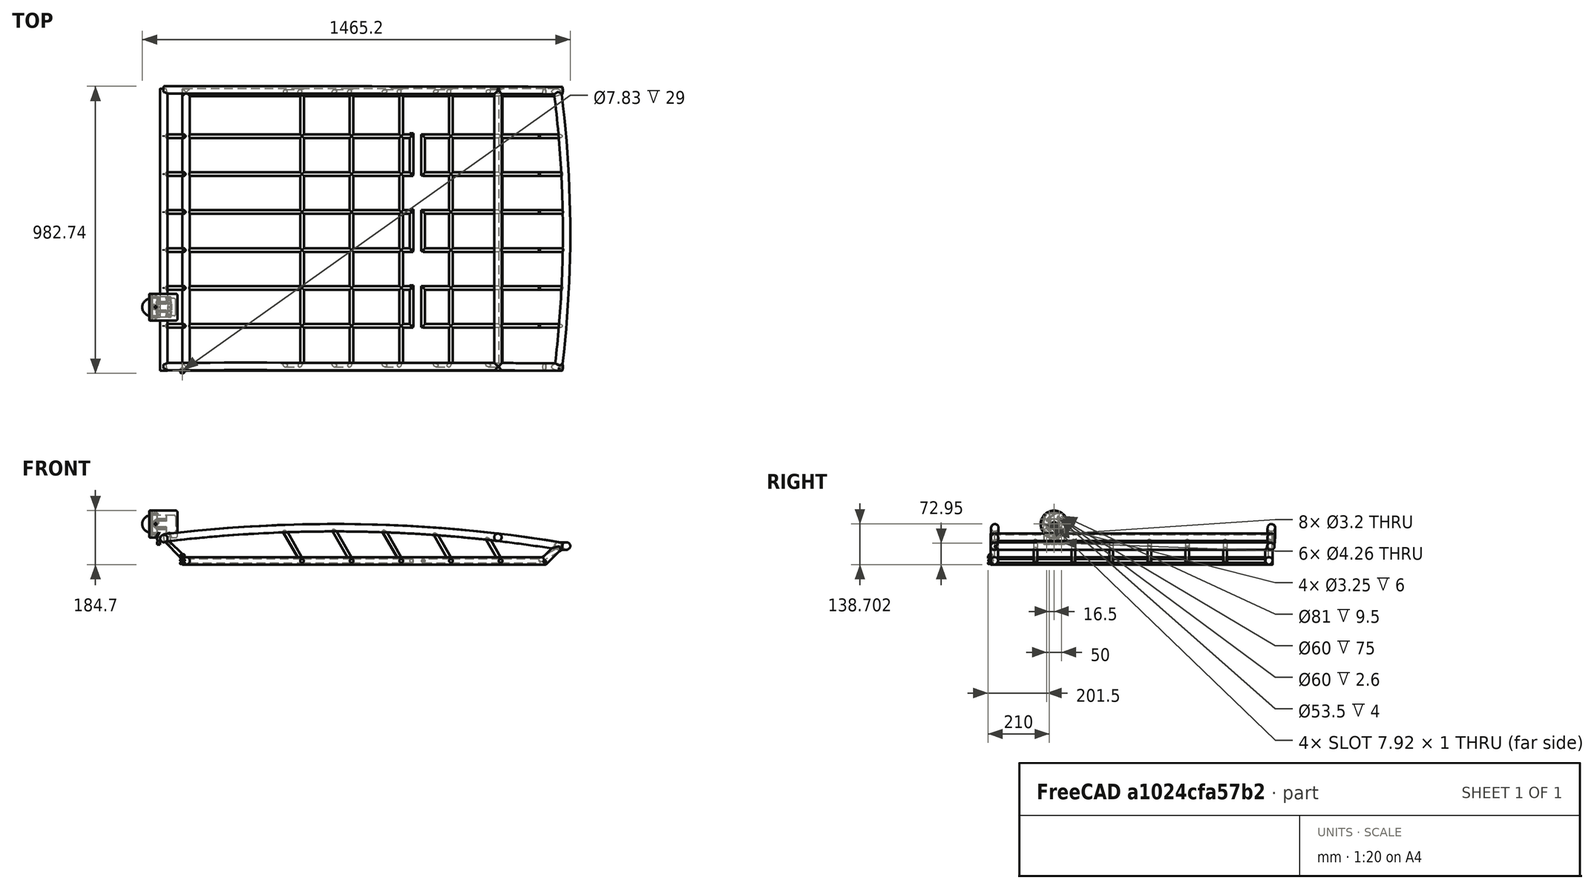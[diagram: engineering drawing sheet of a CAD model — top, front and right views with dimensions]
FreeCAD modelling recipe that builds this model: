
FCSTD DOCUMENT  (FreeCAD 1.0R39285 (Git))
Label: boltCameraMount
License: All rights reserved
LicenseURL: https://en.wikipedia.org/wiki/All_rights_reserved
objects: Part::Cylinder×65, Part::MultiFuse×23, Part::Feature×23, Sketcher::SketchObject×10, Part::Extrusion×10, Part::Cut×10, Part::Torus×3, Part::FeaturePython×2, App::Part×2, Part::Mirroring×2, Part::Sphere×2, Part::Fillet×2
note: 162 computed .brp shape members not serialized (recipe doc carries the construction recipe); baked Part::Feature solids carry a one-line shape summary decoded from their .brp

FEATURE [Part::Cylinder] Cylinder  label="base00"
  Angle = 360
  AttacherType = Attacher::AttachEngine3D
  FirstAngle = 0
  Height = 965.2
  Placement = pos=(12.7,0,0) rot=(-0.57735,0.57735,0.57735;2.0944rad)
  Radius = 12.7
  SecondAngle = 0
FEATURE [Part::Cylinder] Cylinder002  label="base02"
  Angle = 360
  AttacherType = Attacher::AttachEngine3D
  FirstAngle = 0
  Height = 1244.6
  Placement = pos=(0,12.7,0) rot=(0,1,0;1.5708rad)
  Radius = 12.7
  SecondAngle = 0
FEATURE [Part::Cylinder] Cylinder003  label="base03"
  Angle = 360
  AttacherType = Attacher::AttachEngine3D
  FirstAngle = 0
  Height = 1244.6
  Placement = pos=(0,952.5,0) rot=(0,1,0;1.5708rad)
  Radius = 12.7
  SecondAngle = 0
FEATURE [Part::Cylinder] Cylinder004  label="mount01"
  Angle = 360
  AttacherType = Attacher::AttachEngine3D
  FirstAngle = 0
  Height = 76.2
  Placement = pos=(1235.62,12.7,-3.72) rot=(0.382683,0,0.92388;3.14159rad)
  Radius = 12.7
  SecondAngle = 0
FEATURE [Part::Cylinder] Cylinder005  label="mount002"
  Angle = 360
  AttacherType = Attacher::AttachEngine3D
  FirstAngle = 0
  Height = 76.2
  Placement = pos=(1235.62,952.5,-3.72) rot=(0.382683,0,0.92388;3.14159rad)
  Radius = 12.7
  SecondAngle = 0
FEATURE [Part::Cylinder] Cylinder006  label="base004"
  Angle = 360
  AttacherType = Attacher::AttachEngine3D
  FirstAngle = 0
  Height = 965.2
  Placement = pos=(-63.5,0,76.2) rot=(-0.57735,0.57735,0.57735;2.0944rad)
  Radius = 12.7
  SecondAngle = 0
FEATURE [Part::Cylinder] Cylinder007  label="base005"
  Angle = 360
  AttacherType = Attacher::AttachEngine3D
  FirstAngle = 0
  Height = 965.2
  Placement = pos=(1089.2,0,0) rot=(0.57735,-0.57735,-0.57735;4.18879rad)
  Radius = 6.35
  SecondAngle = 0
FEATURE [Part::Cylinder] Cylinder008  label="base006"
  Angle = 360
  AttacherType = Attacher::AttachEngine3D
  FirstAngle = 0
  Height = 965.2
  Placement = pos=(919.2,0,0) rot=(0.57735,-0.57735,-0.57735;4.18879rad)
  Radius = 6.35
  SecondAngle = 0
FEATURE [Part::Cylinder] Cylinder009  label="base007"
  Angle = 360
  AttacherType = Attacher::AttachEngine3D
  FirstAngle = 0
  Height = 965.2
  Placement = pos=(749.2,0,0) rot=(0.57735,-0.57735,-0.57735;4.18879rad)
  Radius = 6.35
  SecondAngle = 0
FEATURE [Part::Cylinder] Cylinder010  label="base008"
  Angle = 360
  AttacherType = Attacher::AttachEngine3D
  FirstAngle = 0
  Height = 965.2
  Placement = pos=(579.2,0,0) rot=(0.57735,-0.57735,-0.57735;4.18879rad)
  Radius = 6.35
  SecondAngle = 0
FEATURE [Part::Cylinder] Cylinder011  label="base009"
  Angle = 360
  AttacherType = Attacher::AttachEngine3D
  FirstAngle = 0
  Height = 965.2
  Placement = pos=(409.2,0,0) rot=(0.57735,-0.57735,-0.57735;4.18879rad)
  Radius = 6.35
  SecondAngle = 0
FEATURE [Part::Cylinder] Cylinder012  label="base010"
  Angle = 360
  AttacherType = Attacher::AttachEngine3D
  FirstAngle = 0
  Height = 790
  Placement = pos=(0,149.7,0) rot=(0,1,0;1.5708rad)
  Radius = 6.35
  SecondAngle = 0
FEATURE [Part::Cylinder] Cylinder013  label="base011"
  Angle = 360
  AttacherType = Attacher::AttachEngine3D
  FirstAngle = 0
  Height = 790
  Placement = pos=(0,279.7,0) rot=(0,1,0;1.5708rad)
  Radius = 6.35
  SecondAngle = 0
FEATURE [Part::Cylinder] Cylinder014  label="base012"
  Angle = 360
  AttacherType = Attacher::AttachEngine3D
  FirstAngle = 0
  Height = 790
  Placement = pos=(0,409.7,0) rot=(0,1,0;1.5708rad)
  Radius = 6.35
  SecondAngle = 0
FEATURE [Part::Cylinder] Cylinder015  label="base013"
  Angle = 360
  AttacherType = Attacher::AttachEngine3D
  FirstAngle = 0
  Height = 790
  Placement = pos=(0,539.7,0) rot=(0,1,0;1.5708rad)
  Radius = 6.35
  SecondAngle = 0
FEATURE [Part::Cylinder] Cylinder016  label="base014"
  Angle = 360
  AttacherType = Attacher::AttachEngine3D
  FirstAngle = 0
  Height = 790
  Placement = pos=(0,669.7,0) rot=(0,1,0;1.5708rad)
  Radius = 6.35
  SecondAngle = 0
FEATURE [Part::Cylinder] Cylinder017  label="base015"
  Angle = 360
  AttacherType = Attacher::AttachEngine3D
  FirstAngle = 0
  Height = 790
  Placement = pos=(0,799.7,0) rot=(0,1,0;1.5708rad)
  Radius = 6.35
  SecondAngle = 0
FEATURE [Part::Cylinder] Cylinder018  label="base016"
  Angle = 360
  AttacherType = Attacher::AttachEngine3D
  FirstAngle = 0
  Height = 141
  Placement = pos=(784.2,148,0) rot=(0.57735,-0.57735,-0.57735;4.18879rad)
  Radius = 6.35
  SecondAngle = 0
FEATURE [Part::Cylinder] Cylinder019  label="base017"
  Angle = 360
  AttacherType = Attacher::AttachEngine3D
  FirstAngle = 0
  Height = 141
  Placement = pos=(784.2,408,0) rot=(0.57735,-0.57735,-0.57735;4.18879rad)
  Radius = 6.35
  SecondAngle = 0
FEATURE [Part::Cylinder] Cylinder020  label="base018"
  Angle = 360
  AttacherType = Attacher::AttachEngine3D
  FirstAngle = 0
  Height = 141
  Placement = pos=(784.2,668,0) rot=(0.57735,-0.57735,-0.57735;4.18879rad)
  Radius = 6.35
  SecondAngle = 0
FEATURE [Part::Cylinder] Cylinder021  label="base019"
  Angle = 360
  AttacherType = Attacher::AttachEngine3D
  FirstAngle = 0
  Height = 400
  Placement = pos=(0,149.7,0) rot=(0,1,0;1.5708rad)
  Radius = 6.35
  SecondAngle = 0
FEATURE [Part::Cylinder] Cylinder022  label="base020"
  Angle = 360
  AttacherType = Attacher::AttachEngine3D
  FirstAngle = 0
  Height = 400
  Placement = pos=(0,279.7,0) rot=(0,1,0;1.5708rad)
  Radius = 6.35
  SecondAngle = 0
FEATURE [Part::Cylinder] Cylinder023  label="base021"
  Angle = 360
  AttacherType = Attacher::AttachEngine3D
  FirstAngle = 0
  Height = 400
  Placement = pos=(0,409.7,0) rot=(0,1,0;1.5708rad)
  Radius = 6.35
  SecondAngle = 0
FEATURE [Part::Cylinder] Cylinder024  label="base022"
  Angle = 360
  AttacherType = Attacher::AttachEngine3D
  FirstAngle = 0
  Height = 400
  Placement = pos=(0,539.7,0) rot=(0,1,0;1.5708rad)
  Radius = 6.35
  SecondAngle = 0
FEATURE [Part::Cylinder] Cylinder025  label="base023"
  Angle = 360
  AttacherType = Attacher::AttachEngine3D
  FirstAngle = 0
  Height = 400
  Placement = pos=(0,669.7,0) rot=(0,1,0;1.5708rad)
  Radius = 6.35
  SecondAngle = 0
FEATURE [Part::Cylinder] Cylinder026  label="base024"
  Angle = 360
  AttacherType = Attacher::AttachEngine3D
  FirstAngle = 0
  Height = 400
  Placement = pos=(0,799.7,0) rot=(0,1,0;1.5708rad)
  Radius = 6.35
  SecondAngle = 0
FEATURE [Part::Cylinder] Cylinder027  label="base025"
  Angle = 360
  AttacherType = Attacher::AttachEngine3D
  FirstAngle = 0
  Height = 141
  Placement = pos=(0,665,0) rot=(0.57735,-0.57735,-0.57735;4.18879rad)
  Radius = 6.35
  SecondAngle = 0
FEATURE [Part::Cylinder] Cylinder028  label="base026"
  Angle = 360
  AttacherType = Attacher::AttachEngine3D
  FirstAngle = 0
  Height = 141
  Placement = pos=(0,405,0) rot=(0.57735,-0.57735,-0.57735;4.18879rad)
  Radius = 6.35
  SecondAngle = 0
FEATURE [Part::Cylinder] Cylinder029  label="base027"
  Angle = 360
  AttacherType = Attacher::AttachEngine3D
  FirstAngle = 0
  Height = 141
  Placement = pos=(0,145,0) rot=(0.57735,-0.57735,-0.57735;4.18879rad)
  Radius = 6.35
  SecondAngle = 0
FEATURE [Part::Cylinder] Cylinder030  label="Cylinder"
  Angle = 360
  AttacherType = Attacher::AttachEngine3D
  FirstAngle = 0
  Height = 124.3
  Placement = pos=(409,19,0) rot=(0,-1,0;0.523599rad)
  Radius = 6.35
  SecondAngle = 0
FEATURE [Part::Cylinder] Cylinder031
  Angle = 360
  AttacherType = Attacher::AttachEngine3D
  FirstAngle = 0
  Height = 131.3
  Placement = pos=(579,19,0) rot=(0,-1,0;0.523599rad)
  Radius = 6.35
  SecondAngle = 0
FEATURE [Part::Cylinder] Cylinder032
  Angle = 360
  AttacherType = Attacher::AttachEngine3D
  FirstAngle = 0
  Height = 124.3
  Placement = pos=(749,19,0) rot=(0,-1,0;0.523599rad)
  Radius = 6.35
  SecondAngle = 0
FEATURE [Part::Cylinder] Cylinder033
  Angle = 360
  AttacherType = Attacher::AttachEngine3D
  FirstAngle = 0
  Height = 117.3
  Placement = pos=(919,19,0) rot=(0,-1,0;0.523599rad)
  Radius = 6.35
  SecondAngle = 0
FEATURE [Part::Cylinder] Cylinder034
  Angle = 360
  AttacherType = Attacher::AttachEngine3D
  FirstAngle = 0
  Height = 96.3
  Placement = pos=(1089,19,0) rot=(0,-1,0;0.523599rad)
  Radius = 6.35
  SecondAngle = 0
FEATURE [Part::Cylinder] Cylinder035
  Angle = 360
  AttacherType = Attacher::AttachEngine3D
  FirstAngle = 0
  Height = 124.3
  Placement = pos=(409,19,0) rot=(0,-1,0;0.523599rad)
  Radius = 6.35
  SecondAngle = 0
FEATURE [Part::Cylinder] Cylinder036
  Angle = 360
  AttacherType = Attacher::AttachEngine3D
  FirstAngle = 0
  Height = 131.3
  Placement = pos=(579,19,0) rot=(0,-1,0;0.523599rad)
  Radius = 6.35
  SecondAngle = 0
FEATURE [Part::Cylinder] Cylinder037
  Angle = 360
  AttacherType = Attacher::AttachEngine3D
  FirstAngle = 0
  Height = 124.3
  Placement = pos=(749,19,0) rot=(0,-1,0;0.523599rad)
  Radius = 6.35
  SecondAngle = 0
FEATURE [Part::Cylinder] Cylinder038
  Angle = 360
  AttacherType = Attacher::AttachEngine3D
  FirstAngle = 0
  Height = 117.3
  Placement = pos=(919,19,0) rot=(0,-1,0;0.523599rad)
  Radius = 6.35
  SecondAngle = 0
FEATURE [Part::Cylinder] Cylinder039
  Angle = 360
  AttacherType = Attacher::AttachEngine3D
  FirstAngle = 0
  Height = 96.3
  Placement = pos=(1089,19,0) rot=(0,-1,0;0.523599rad)
  Radius = 6.35
  SecondAngle = 0
FEATURE [Part::Cylinder] Cylinder040 .. Cylinder044  x5 (patterned run collapsed; names and placements below)
  Angle = 360
  AttacherType = Attacher::AttachEngine3D
  FirstAngle = 0
  Height = 124.3
  Radius = 6.35
  SecondAngle = 0
  placements: 5 in arithmetic series — first pos=(17.6777,152.7,-3.53553) rot=(0,-1,0;0.785398rad), step (0,130,0), last pos=(17.6777,672.7,-3.53553) rot=(0,-1,0;0.785398rad)
FEATURE [Part::Cylinder] Cylinder045
  Angle = 360
  AttacherType = Attacher::AttachEngine3D
  FirstAngle = 0
  Height = 100.3
  Placement = pos=(17.6777,152.7,-3.53553) rot=(0,-1,0;0.785398rad)
  Radius = 6.35
  SecondAngle = 0
FEATURE [Part::Cylinder] Cylinder046 .. Cylinder050  x5 (patterned run collapsed; names and placements below)
  Angle = 360
  AttacherType = Attacher::AttachEngine3D
  FirstAngle = 0
  Height = 100
  Radius = 6.35
  SecondAngle = 0
  placements: 5 in arithmetic series — first pos=(17.6777,282.7,-3.53553) rot=(0,-1,0;0.785398rad), step (0,130,0), last pos=(17.6777,802.7,-3.53553) rot=(0,-1,0;0.785398rad)
FEATURE [Part::Cylinder] Cylinder051
  Angle = 360
  AttacherType = Attacher::AttachEngine3D
  FirstAngle = 0
  Height = 124.3
  Placement = pos=(17.6777,802.7,-3.53553) rot=(0,-1,0;0.785398rad)
  Radius = 6.35
  SecondAngle = 0
FEATURE [Part::Cylinder] Cylinder052  label="base028"
  Angle = 360
  AttacherType = Attacher::AttachEngine3D
  FirstAngle = 0
  Height = 965.2
  Placement = pos=(1080,0,80.5) rot=(-0.57735,0.57735,0.57735;2.0944rad)
  Radius = 12.7
  SecondAngle = 0
FEATURE [Part::MultiFuse] Fusion001  label="vertical"
  Shapes = -> [Cylinder007,Cylinder008,Cylinder009,Cylinder010,Cylinder011]
FEATURE [Part::MultiFuse] Fusion002  label="horizontal"
  Placement = pos=(0,3,0) rot=(0,0,1;0rad)
  Shapes = -> [Cylinder012,Cylinder013,Cylinder014,Cylinder015,Cylinder016,Cylinder017,Cylinder018,Cylinder019,Cylinder020]
FEATURE [Part::MultiFuse] Fusion003  label="horizontal_front"
  Placement = pos=(824,3,0) rot=(0,0,1;0rad)
  Shapes = -> [Cylinder025,Cylinder026,Cylinder022,Cylinder021,Cylinder023,Cylinder024,Cylinder027,Cylinder029,Cylinder028]
FEATURE [Part::MultiFuse] Fusion004  label="side_bars_1"
  Shapes = -> [Cylinder030,Cylinder031,Cylinder032,Cylinder033,Cylinder034]
FEATURE [Part::MultiFuse] Fusion005  label="side_bars_002"
  Placement = pos=(0,936.4,0) rot=(0,0,1;0rad)
  Shapes = -> [Cylinder035,Cylinder036,Cylinder037,Cylinder038,Cylinder039]
FEATURE [Part::MultiFuse] Fusion006  label="Back_bars"
  Shapes = -> [Cylinder040,Cylinder041,Cylinder042,Cylinder043,Cylinder044,Cylinder051]
FEATURE [Part::MultiFuse] Fusion007  label="front_bar"
  Placement = pos=(1229,0,16) rot=(0,1,0;1.8326rad)
  Shapes = -> [Cylinder045,Cylinder046,Cylinder047,Cylinder048,Cylinder049,Cylinder050]
FEATURE [Part::Torus] Torus
  Angle1 = -180
  Angle2 = 180
  Angle3 = 14.3
  AttacherType = Attacher::AttachEngine3D
  Placement = pos=(-2495,471.5,50.8) rot=(0,0,-1;0.122173rad)
  Radius1 = 3810
  Radius2 = 12.7
FEATURE [Part::Torus] Torus001
  Angle1 = -180
  Angle2 = 180
  Angle3 = 16.28
  AttacherType = Attacher::AttachEngine3D
  Placement = pos=(519.042,-57.4562,-4703.18) rot=(0.533716,0.602162,0.593758;4.10898rad)
  Radius1 = 4817.1
  Radius2 = 12.7
FEATURE [Part::Torus] Torus002
  Angle1 = -180
  Angle2 = 180
  Angle3 = 16.28
  AttacherType = Attacher::AttachEngine3D
  Placement = pos=(519.042,889,-4703.18) rot=(0.533716,0.602162,0.593758;4.10898rad)
  Radius1 = 4817.1
  Radius2 = 12.7
FEATURE [Part::MultiFuse] Fusion  label="out_frame"
  Shapes = -> [Cylinder,Cylinder002,Cylinder003,Cylinder005,Cylinder004,Torus,Cylinder006,Torus001,Torus002,Cylinder052]
FEATURE [Part::MultiFuse] Fusion011  label="Car_frame"
  Shapes = -> [Fusion,Fusion001,Fusion002,Fusion003,Fusion004,Fusion005,Fusion006,Fusion007]
FEATURE [Sketcher::SketchObject] Sketch
  ArcFitTolerance = 1e-06
  FullyConstrained = true
  MakeInternals = false
  Placement = pos=(0,0,0) rot=(1,0,0;1.5708rad)
  sketch-geometry (10):
    g0: ArcOfCircle CenterX=0 CenterY=0 CenterZ=0 NormalX=0 NormalY=0 NormalZ=1 AngleXU=0 Radius=13.25 StartAngle=6.28318 EndAngle=9.42478
    g1: ArcOfCircle CenterX=0 CenterY=0 CenterZ=0 NormalX=0 NormalY=0 NormalZ=1 AngleXU=0 Radius=23 StartAngle=5.8031 EndAngle=9.90486
    g2: LineSegment StartX=-20.4 StartY=-10.6226 StartZ=0 EndX=-23.25 EndY=-10.6226 EndZ=0
    g3: LineSegment StartX=-23.25 StartY=-10.6226 StartZ=0 EndX=-23.25 EndY=-20.6226 EndZ=0
    g4: LineSegment StartX=-23.25 StartY=-20.6226 StartZ=0 EndX=-13.25 EndY=-20.6226 EndZ=0
    g5: LineSegment StartX=20.4 StartY=-10.6226 StartZ=0 EndX=23.25 EndY=-10.6226 EndZ=0
    g6: LineSegment StartX=23.25 StartY=-10.6226 StartZ=0 EndX=23.25 EndY=-20.6226 EndZ=0
    g7: LineSegment StartX=23.25 StartY=-20.6226 StartZ=0 EndX=13.25 EndY=-20.6226 EndZ=0
    g8: LineSegment StartX=13.25 StartY=-20.6226 StartZ=0 EndX=13.25 EndY=-2.78003e-05 EndZ=0
    g9: LineSegment StartX=-13.25 StartY=-20.6226 StartZ=0 EndX=-13.25 EndY=-2.78003e-05 EndZ=0
  constraints (29):
    c: Coincident(g0,g-1)
    c: Coincident(g1,g0)
    c: Coincident(g2,g1)
    c: Horizontal(g2)
    c: Coincident(g3,g2)
    c: Vertical(g3)
    c: Coincident(g4,g3)
    c: Horizontal(g4)
    c: Coincident(g5,g1)
    c: Horizontal(g5)
    c: Coincident(g6,g5)
    c: Vertical(g6)
    c: Coincident(g7,g6)
    c: Horizontal(g7)
    c: Diameter(g0) = 26.5
    c: Diameter(g1) = 46
    c: DistanceY(g3,g3) = 10
    c: DistanceY(g6,g6) = 10
    c: DistanceX(g7,g7) = 10
    c: DistanceX(g4,g4) = 10
    c: Distance(g2,g2) = 2.85
    c: Coincident(g8,g7)
    c: Coincident(g8,g0)
    c: Coincident(g9,g4)
    c: Coincident(g9,g0)
    c: Vertical(g8)
    c: Vertical(g9)
    c: Symmetric(g4,g7,g-2)
    c: DistanceX(g0,g0) = 26.5
FEATURE [Part::Extrusion] Extrude  label="CamHold"
  Base = -> Sketch
  Dir = (0,-1,2e-16)
  DirMode = 2
  FaceMakerClass = Part::FaceMakerBullseye
  FaceMakerMode = 3
  LengthFwd = 20
  LengthRev = 0
  Placement = pos=(0,-15,0) rot=(0,0,1;0rad)
  Solid = true
  Symmetric = false
FEATURE [Part::FeaturePython] Tube  # WARN: FeaturePython — macro-defined, semantics opaque (R4)
  AttacherType = Attacher::AttachEngine3D
  Height = 80
  InnerRadius = 30
  OuterRadius = 46
  Placement = pos=(40,-50,50) rot=(0,1,0;4.71239rad)
FEATURE [Part::Cylinder] Cylinder059
  Angle = 360
  AttacherType = Attacher::AttachEngine3D
  FirstAngle = 0
  Height = 150
  Placement = pos=(0,-125,0) rot=(1,0,0;4.71239rad)
  Radius = 13.25
  SecondAngle = 0
FEATURE [Part::Cut] Cut  label="CylinderCam"
  Base = -> Tube
  Refine = true
  Tool = -> Cylinder059
FEATURE [Sketcher::SketchObject] Sketch004
  ArcFitTolerance = 1e-06
  FullyConstrained = true
  MakeInternals = false
  Placement = pos=(0,0,0) rot=(1,0,0;1.5708rad)
  sketch-geometry (10):
    g0: ArcOfCircle CenterX=0 CenterY=0 CenterZ=0 NormalX=0 NormalY=0 NormalZ=1 AngleXU=0 Radius=13.25 StartAngle=6.28319 EndAngle=9.42478
    g1: ArcOfCircle CenterX=0 CenterY=0 CenterZ=0 NormalX=0 NormalY=0 NormalZ=1 AngleXU=0 Radius=23 StartAngle=5.8031 EndAngle=9.90486
    g2: LineSegment StartX=-20.4 StartY=-10.6226 StartZ=0 EndX=-23.25 EndY=-10.6226 EndZ=0
    g3: LineSegment StartX=-23.25 StartY=-10.6226 StartZ=0 EndX=-23.25 EndY=-20.6226 EndZ=0
    g4: LineSegment StartX=-23.25 StartY=-20.6226 StartZ=0 EndX=-13.25 EndY=-20.6226 EndZ=0
    g5: LineSegment StartX=20.4 StartY=-10.6226 StartZ=0 EndX=23.25 EndY=-10.6226 EndZ=0
    g6: LineSegment StartX=23.25 StartY=-10.6226 StartZ=0 EndX=23.25 EndY=-20.6226 EndZ=0
    g7: LineSegment StartX=23.25 StartY=-20.6226 StartZ=0 EndX=13.25 EndY=-20.6226 EndZ=0
    g8: LineSegment StartX=-13.25 StartY=-20.6226 StartZ=0 EndX=-13.25 EndY=-4.29509e-07 EndZ=0
    g9: LineSegment StartX=13.25 StartY=-20.6226 StartZ=0 EndX=13.25 EndY=-3.97031e-07 EndZ=0
  constraints (29):
    c: Coincident(g0,g-1)
    c: Coincident(g1,g0)
    c: Coincident(g2,g1)
    c: Horizontal(g2)
    c: Coincident(g3,g2)
    c: Vertical(g3)
    c: Coincident(g4,g3)
    c: Horizontal(g4)
    c: Coincident(g5,g1)
    c: Horizontal(g5)
    c: Coincident(g6,g5)
    c: Vertical(g6)
    c: Coincident(g7,g6)
    c: Horizontal(g7)
    c: Diameter(g0) = 26.5
    c: Diameter(g1) = 46
    c: DistanceY(g3,g3) = 10
    c: DistanceY(g6,g6) = 10
    c: DistanceX(g7,g7) = 10
    c: DistanceX(g4,g4) = 10
    c: Distance(g2,g2) = 2.85
    c: Coincident(g8,g4)
    c: Coincident(g8,g0)
    c: Coincident(g9,g7)
    c: Coincident(g9,g0)
    c: Vertical(g8)
    c: Vertical(g9)
    c: Symmetric(g4,g7,g-2)
    c: DistanceX(g0,g0) = 26.5
FEATURE [Part::Extrusion] Extrude004  label="CamHold001"
  Base = -> Sketch004
  Dir = (0,-1,2e-16)
  DirMode = 2
  FaceMakerClass = Part::FaceMakerBullseye
  FaceMakerMode = 3
  LengthFwd = 20
  LengthRev = 0
  Placement = pos=(0,-40,0) rot=(0,0,1;0rad)
  Solid = true
  Symmetric = false
FEATURE [Sketcher::SketchObject] Sketch005
  ArcFitTolerance = 1e-06
  FullyConstrained = true
  MakeInternals = false
  Placement = pos=(0,0,0) rot=(1,0,0;1.5708rad)
  sketch-geometry (10):
    g0: ArcOfCircle CenterX=0 CenterY=0 CenterZ=0 NormalX=0 NormalY=0 NormalZ=1 AngleXU=0 Radius=13.25 StartAngle=6.28319 EndAngle=9.42478
    g1: ArcOfCircle CenterX=0 CenterY=0 CenterZ=0 NormalX=0 NormalY=0 NormalZ=1 AngleXU=0 Radius=23 StartAngle=5.8031 EndAngle=9.90486
    g2: LineSegment StartX=-20.4 StartY=-10.6226 StartZ=0 EndX=-23.25 EndY=-10.6226 EndZ=0
    g3: LineSegment StartX=-23.25 StartY=-10.6226 StartZ=0 EndX=-23.25 EndY=-20.6226 EndZ=0
    g4: LineSegment StartX=-23.25 StartY=-20.6226 StartZ=0 EndX=-13.25 EndY=-20.6226 EndZ=0
    g5: LineSegment StartX=20.4 StartY=-10.6226 StartZ=0 EndX=23.25 EndY=-10.6226 EndZ=0
    g6: LineSegment StartX=23.25 StartY=-10.6226 StartZ=0 EndX=23.25 EndY=-20.6226 EndZ=0
    g7: LineSegment StartX=23.25 StartY=-20.6226 StartZ=0 EndX=13.25 EndY=-20.6226 EndZ=0
    g8: LineSegment StartX=-13.25 StartY=-20.6226 StartZ=0 EndX=-13.25 EndY=-4.19512e-07 EndZ=0
    g9: LineSegment StartX=13.25 StartY=-20.6226 StartZ=0 EndX=13.25 EndY=-4.07791e-07 EndZ=0
  constraints (29):
    c: Coincident(g0,g-1)
    c: Coincident(g1,g0)
    c: Coincident(g2,g1)
    c: Horizontal(g2)
    c: Coincident(g3,g2)
    c: Vertical(g3)
    c: Coincident(g4,g3)
    c: Horizontal(g4)
    c: Coincident(g5,g1)
    c: Horizontal(g5)
    c: Coincident(g6,g5)
    c: Vertical(g6)
    c: Coincident(g7,g6)
    c: Horizontal(g7)
    c: Diameter(g0) = 26.5
    c: Diameter(g1) = 46
    c: DistanceY(g3,g3) = 10
    c: DistanceY(g6,g6) = 10
    c: DistanceX(g7,g7) = 10
    c: DistanceX(g4,g4) = 10
    c: Distance(g2,g2) = 2.85
    c: Coincident(g8,g4)
    c: Coincident(g8,g0)
    c: Coincident(g9,g7)
    c: Coincident(g9,g0)
    c: Vertical(g8)
    c: Vertical(g9)
    c: Symmetric(g4,g7,g-2)
    c: DistanceX(g0,g0) = 26.5
FEATURE [Part::Extrusion] Extrude005  label="CamHold002"
  Base = -> Sketch005
  Dir = (0,-1,2e-16)
  DirMode = 2
  FaceMakerClass = Part::FaceMakerBullseye
  FaceMakerMode = 3
  LengthFwd = 20
  LengthRev = 0
  Placement = pos=(0,-65,0) rot=(0,0,1;0rad)
  Solid = true
  Symmetric = false
FEATURE [Part::Cylinder] Cylinder060
  Angle = 360
  AttacherType = Attacher::AttachEngine3D
  FirstAngle = 0
  Height = 97
  Placement = pos=(45,-50,50) rot=(0,1,0;4.71239rad)
  Radius = 30
  SecondAngle = 0
FEATURE [Part::MultiFuse] Fusion019  label="CamHolder"
  Refine = true
  Shapes = -> [Cut,Extrude,Extrude004,Extrude005]
FEATURE [Part::Cut] Cut001  label="CameraHold"
  Base = -> Fusion019
  Placement = pos=(-63.5,267,76) rot=(0,0,1;0rad)
  Refine = true
  Tool = -> Cylinder060
FEATURE [Part::Feature] Part__Feature228  label="Camera"
  Placement = pos=(-89,217,126) rot=(0,1,0;4.71239rad)
  shape: bbox 25.12 x 38 x 38 mm, 164 faces (baked)
FEATURE [Part::Cylinder] Cylinder061  label="BackCover"
  Angle = 360
  AttacherType = Attacher::AttachEngine3D
  FirstAngle = 0
  Height = 6
  Placement = pos=(-17.5,217,126) rot=(0,1,0;4.71239rad)
  Radius = 46
  SecondAngle = 0
FEATURE [Part::Feature] Part__Feature229  label="Body008"
  shape: bbox 15.5 x 16.75 x 29 mm, 21 faces (baked)
FEATURE [Part::Feature] Part__Feature230  label="Body009"
  Placement = pos=(0,0,2) rot=(0,0,1;0rad)
  shape: bbox 17.44 x 17.44 x 14.25 mm, 14 faces (baked)
FEATURE [Part::Feature] Part__Feature231  label="Body010"
  Placement = pos=(0,0,-5.5) rot=(0,0,1;0rad)
  shape: bbox 19 x 19 x 4.75 mm, 25 faces (baked)
FEATURE [Part::Feature] Part__Feature232  label="Body011"
  shape: bbox 16.75 x 16.75 x 0.9 mm, 4 faces (baked)
FEATURE [App::Part] PG7_Gland003  label="PG7_Gland"
  Group = -> [Part__Feature229,Part__Feature230,Part__Feature231,Part__Feature232]
  Origin = -> Origin046
  Placement = pos=(-17.5,217,126.031) rot=(-0.58919,-0.56024,-0.582225;4.17783rad)
FEATURE [Part::Cylinder] Cylinder062
  Angle = 360
  AttacherType = Attacher::AttachEngine3D
  FirstAngle = 0
  Height = 2.6
  Radius = 40
  SecondAngle = 0
FEATURE [Part::Cylinder] Cylinder001  label="Cylinder_in"
  Angle = 360
  AttacherType = Attacher::AttachEngine3D
  FirstAngle = 0
  Height = 2.6
  Radius = 30
  SecondAngle = 0
FEATURE [Part::Cut] Cut003  label="Base_flat"
  Base = -> Cylinder062
  Tool = -> Cylinder001
FEATURE [Part::Cylinder] Cylinder063 .. Cylinder066  x4 (patterned run collapsed; names and placements below)
  Angle = 360
  AttacherType = Attacher::AttachEngine3D
  FirstAngle = 0
  Height = 10
  Radius = 1.6
  SecondAngle = 0
  placements: all 4 at pos=(35.5,0,0) rot=(0,0,1;0rad)
FEATURE [Part::Mirroring] Part__Mirroring  label="Cylinder003 (Mirror #1)"
  Base = (0,0,0)
  Normal = (1,0,0)
  Source = -> Cylinder064
FEATURE [Part::MultiFuse] Fusion178  label="hole01"
  Shapes = -> [Cylinder063,Part__Mirroring]
FEATURE [Part::Mirroring] Part__Mirroring001  label="Cylinder003 (Mirror #1)001"
  Base = (0,0,0)
  Normal = (1,0,0)
  Source = -> Cylinder066
FEATURE [Part::MultiFuse] Fusion020  label="hole002"
  Placement = pos=(0,0,0) rot=(0,0,1;1.5708rad)
  Shapes = -> [Cylinder065,Part__Mirroring001]
FEATURE [Part::MultiFuse] Fusion021  label="Holes"
  Placement = pos=(0,0,-4) rot=(0,0,1;0rad)
  Shapes = -> [Fusion178,Fusion020]
FEATURE [Part::Cut] Cut004
  Base = -> Cut003
  Tool = -> Fusion021
FEATURE [Part::Sphere] Sphere  label="Sphere_out"
  Angle1 = -90
  Angle2 = 90
  Angle3 = 180
  AttacherType = Attacher::AttachEngine3D
  Placement = pos=(0,0,0) rot=(1,0,0;1.5708rad)
  Radius = 30
FEATURE [Part::Sphere] Sphere001  label="Sphere_in"
  Angle1 = -90
  Angle2 = 90
  Angle3 = 180
  AttacherType = Attacher::AttachEngine3D
  Placement = pos=(0,0,0) rot=(1,0,0;1.5708rad)
  Radius = 28.7
FEATURE [Part::Cut] Cut002  label="Dome"
  Base = -> Sphere
  Tool = -> Sphere001
FEATURE [Part::MultiFuse] Fusion022  label="lightDome"
  Placement = pos=(-107.5,217,126) rot=(0,1,0;4.71239rad)
  Shapes = -> [Cut002,Cut004]
FEATURE [Sketcher::SketchObject] Sketch425
  ArcFitTolerance = 0
  FullyConstrained = true
  MakeInternals = false
  Placement = pos=(0,0,-20) rot=(0,0,1;0rad)
  sketch-geometry (12):
    g0: ArcOfCircle CenterX=-20 CenterY=-290 CenterZ=0 NormalX=0 NormalY=0 NormalZ=1 AngleXU=0 Radius=10 StartAngle=5.49779 EndAngle=8.63938
    g1: ArcOfCircle CenterX=20 CenterY=-290 CenterZ=0 NormalX=0 NormalY=0 NormalZ=1 AngleXU=0 Radius=10 StartAngle=0.785398 EndAngle=3.92699
    g2: ArcOfCircle CenterX=20 CenterY=-250 CenterZ=0 NormalX=0 NormalY=0 NormalZ=1 AngleXU=0 Radius=10 StartAngle=2.35619 EndAngle=5.49779
    g3: ArcOfCircle CenterX=-20 CenterY=-250 CenterZ=0 NormalX=0 NormalY=0 NormalZ=1 AngleXU=0 Radius=10 StartAngle=3.92699 EndAngle=7.06858
    g4: ArcOfCircle CenterX=0 CenterY=-270 CenterZ=0 NormalX=0 NormalY=0 NormalZ=1 AngleXU=0 Radius=30 StartAngle=2.01636 EndAngle=2.69603
    g5: ArcOfCircle CenterX=0 CenterY=-270 CenterZ=0 NormalX=0 NormalY=0 NormalZ=1 AngleXU=0 Radius=30 StartAngle=0.445561 EndAngle=1.12524
    g6: ArcOfCircle CenterX=0 CenterY=-270 CenterZ=0 NormalX=0 NormalY=0 NormalZ=1 AngleXU=0 Radius=30 StartAngle=5.15795 EndAngle=5.83762
    g7: ArcOfCircle CenterX=0 CenterY=-270 CenterZ=0 NormalX=0 NormalY=0 NormalZ=1 AngleXU=0 Radius=30 StartAngle=3.58715 EndAngle=4.26683
    g8: Circle CenterX=-17 CenterY=-253 CenterZ=0 NormalX=0 NormalY=0 NormalZ=1 AngleXU=0 Radius=1.6
    g9: Circle CenterX=17 CenterY=-253 CenterZ=0 NormalX=0 NormalY=0 NormalZ=1 AngleXU=0 Radius=1.6
    g10: Circle CenterX=17 CenterY=-287 CenterZ=0 NormalX=0 NormalY=0 NormalZ=1 AngleXU=0 Radius=1.6
    g11: Circle CenterX=-17 CenterY=-287 CenterZ=0 NormalX=0 NormalY=0 NormalZ=1 AngleXU=0 Radius=1.6
  constraints (41):
    c: Vertical(g0,g3)
    c: Vertical(g1,g2)
    c: Horizontal(g2,g3)
    c: Horizontal(g1,g0)
    c: Equal(g2,g3)
    c: Equal(g2,g0)
    c: Equal(g2,g1)
    c: Diameter(g2) = 20
    c: Horizontal(g0,g1)
    c: Horizontal(g1,g0)
    c: Angle(g0) = 3.14159
    c: Vertical(g0,g3)
    c: Vertical(g0,g3)
    c: Angle(g2) = 3.14159
    c: DistanceY(g0) = -290
    c: Coincident(g4,g3)
    c: Coincident(g4,g3)
    c: Coincident(g5,g4)
    c: Coincident(g5,g2)
    c: Coincident(g5,g2)
    c: Coincident(g6,g4)
    c: Coincident(g6,g1)
    c: Coincident(g6,g1)
    c: Coincident(g7,g4)
    c: Coincident(g7,g0)
    c: Coincident(g7,g0)
    c: DistanceX(g4) = 0
    c: DistanceY(g4) = -270
    c: DistanceX(g0,g4) = 20
    c: DistanceX(g11,g4) = 17
    c: DistanceY(g11,g4) = 17
    c: DistanceX(g4,g10) = 17
    c: DistanceY(g10,g4) = 17
    c: DistanceX(g4,g9) = 17
    c: Vertical(g8,g11)
    c: Horizontal(g8,g9)
    c: DistanceY(g4,g8) = 17
    c: Equal(g10,g9)
    c: Equal(g10,g8)
    c: Equal(g10,g11)
    c: Diameter(g10) = 3.2
FEATURE [Part::Extrusion] Extrude201  label="cameraHold003"
  Base = -> Sketch425
  Dir = (0,0,1)
  DirMode = 2
  FaceMakerClass = Part::FaceMakerBullseye
  FaceMakerMode = 3
  LengthFwd = 31
  LengthRev = 0
  Placement = pos=(-66.5,487,126) rot=(0,-1,0;4.71239rad)
  Solid = true
  Symmetric = false
FEATURE [Part::Cylinder] Cylinder067  label="BackHole"
  Angle = 360
  AttacherType = Attacher::AttachEngine3D
  FirstAngle = 0
  Height = 20
  Placement = pos=(-8.5,217,126) rot=(0,1,0;4.71239rad)
  Radius = 6.5
  SecondAngle = 0
FEATURE [Part::MultiFuse] Fusion297  label="HolderCovered"
  Refine = true
  Shapes = -> [Cut001,Cylinder061]
FEATURE [Part::Cut] Cut160  label="HolderCovered001"
  Base = -> Fusion297
  Refine = true
  Tool = -> Cylinder067
FEATURE [Part::MultiFuse] Fusion298  label="CameraHold001"
  Refine = true
  Shapes = -> [Cut160,Extrude201]
FEATURE [Part::FeaturePython] Tube001  label="TopGuard"  # WARN: FeaturePython — macro-defined, semantics opaque (R4)
  AttacherType = Attacher::AttachEngine3D
  Height = 11
  InnerRadius = 40.5
  OuterRadius = 46
  Placement = pos=(-103,217,126) rot=(0,1,0;4.71239rad)
FEATURE [Sketcher::SketchObject] Sketch426
  ArcFitTolerance = 1e-06
  FullyConstrained = true
  MakeInternals = false
  sketch-geometry (2):
    g0: Circle CenterX=0 CenterY=0 CenterZ=0 NormalX=0 NormalY=0 NormalZ=1 AngleXU=0 Radius=26.75
    g1: Circle CenterX=0 CenterY=0 CenterZ=0 NormalX=0 NormalY=0 NormalZ=1 AngleXU=0 Radius=36.25
  constraints (4):
    c: Coincident(g0,g-1)
    c: Coincident(g1,g0)
    c: Diameter(g0) = 53.5  '73'
    c: Diameter(g1) = 72.5
FEATURE [Part::Extrusion] Extrude202  label="Rubber_Seal"
  Base = -> Sketch426
  Dir = (0,0,1)
  DirMode = 2
  FaceMakerClass = Part::FaceMakerBullseye
  FaceMakerMode = 3
  LengthFwd = 4
  LengthRev = 0
  Placement = pos=(-107.5,217,126.002) rot=(0,-1,0;4.71239rad)
  Solid = true
  Symmetric = false
FEATURE [Part::MultiFuse] Fusion299  label="GuardedCamHolder"
  Refine = true
  Shapes = -> [Fusion298,Tube001]
FEATURE [Part::Feature] Part__Feature233  label="m4_1"
  Placement = pos=(-37,192,60.25) rot=(0,1,0;1.5708rad)
  shape: bbox 54.15 x 7.001 x 7.001 mm, 147 faces (baked)
FEATURE [Part::Feature] Part__Feature234  label="m4_2"
  Placement = pos=(-37,217,60.25) rot=(0,1,0;1.5708rad)
  shape: bbox 54.15 x 7.001 x 7.001 mm, 147 faces (baked)
FEATURE [Part::Feature] Part__Feature235  label="m4_3"
  Placement = pos=(-37,242,60.25) rot=(0,1,0;1.5708rad)
  shape: bbox 54.15 x 7.001 x 7.001 mm, 147 faces (baked)
FEATURE [Part::Feature] Part__Feature236  label="m4Nut1"
  Placement = pos=(-41.25,192,60.25) rot=(0,1,0;4.71239rad)
  shape: bbox 3.764 x 8.084 x 8.084 mm, 38 faces (baked)
FEATURE [Sketcher::SketchObject] Sketch427
  ArcFitTolerance = 1e-06
  FullyConstrained = true
  MakeInternals = false
  Placement = pos=(0,0,0) rot=(-0.57735,0.57735,0.57735;4.18879rad)
  sketch-geometry (7):
    g0: LineSegment StartX=2.25002 StartY=3.8971 StartZ=0 EndX=-2.24998 EndY=3.89713 EndZ=0
    g1: LineSegment StartX=-2.24998 StartY=3.89713 StartZ=0 EndX=-4.5 EndY=2.65295e-05 EndZ=0
    g2: LineSegment StartX=-4.5 StartY=2.65295e-05 StartZ=0 EndX=-2.25002 EndY=-3.8971 EndZ=0
    g3: LineSegment StartX=-2.25002 StartY=-3.8971 StartZ=0 EndX=2.24998 EndY=-3.89713 EndZ=0
    g4: LineSegment StartX=2.24998 StartY=-3.89713 StartZ=0 EndX=4.5 EndY=-2.65295e-05 EndZ=0
    g5: LineSegment StartX=4.5 StartY=-2.65295e-05 StartZ=0 EndX=2.25002 EndY=3.8971 EndZ=0
    g6: Circle [constr] CenterX=0 CenterY=0 CenterZ=0 NormalX=0 NormalY=0 NormalZ=1 AngleXU=0 Radius=4.5
  constraints (16):
    c: Coincident(g0,g1)
    c: Coincident(g1,g2)
    c: Coincident(g2,g3)
    c: Coincident(g3,g4)
    c: Coincident(g4,g5)
    c: Coincident(g5,g0)
    c: Equal(g0, g1-g5) x5
    c: PointOnObject(g0,g6)
    c: PointOnObject(g1,g6)
    c: PointOnObject(g2,g6)
    c: PointOnObject(g3,g6)
    c: PointOnObject(g4,g6)
    c: PointOnObject(g5,g6)
    c: Coincident(g6,g-1)
    c: Radius(g6) = 4.5
    c: DistanceX(g0,g0) = 4.5
FEATURE [Part::Extrusion] Extrude203  label="m4NutCut1"
  Base = -> Sketch427
  Dir = (-1,0,0)
  DirMode = 2
  FaceMakerClass = Part::FaceMakerBullseye
  FaceMakerMode = 3
  LengthFwd = 3
  LengthRev = 0
  Placement = pos=(-40,192,60.25) rot=(0,0,1;0rad)
  Solid = true
  Symmetric = false
FEATURE [Part::Cylinder] Cylinder068  label="m4cyl1"
  Angle = 360
  AttacherType = Attacher::AttachEngine3D
  FirstAngle = 0
  Height = 53
  Placement = pos=(-37,192,60.25) rot=(0,1,0;4.71239rad)
  Radius = 2.13
  SecondAngle = 0
FEATURE [Part::Cylinder] Cylinder069  label="m4cyl2"
  Angle = 360
  AttacherType = Attacher::AttachEngine3D
  FirstAngle = 0
  Height = 53
  Placement = pos=(-37,217,60.25) rot=(0,1,0;4.71239rad)
  Radius = 2.13
  SecondAngle = 0
FEATURE [Part::Cylinder] Cylinder070  label="m4cyl3"
  Angle = 360
  AttacherType = Attacher::AttachEngine3D
  FirstAngle = 0
  Height = 53
  Placement = pos=(-37,242,60.25) rot=(0,1,0;4.71239rad)
  Radius = 2.13
  SecondAngle = 0
FEATURE [Sketcher::SketchObject] Sketch428
  ArcFitTolerance = 1e-06
  FullyConstrained = true
  MakeInternals = false
  Placement = pos=(0,0,0) rot=(-0.57735,0.57735,0.57735;4.18879rad)
  sketch-geometry (7):
    g0: LineSegment StartX=2.25002 StartY=3.8971 StartZ=0 EndX=-2.24998 EndY=3.89713 EndZ=0
    g1: LineSegment StartX=-2.24998 StartY=3.89713 StartZ=0 EndX=-4.5 EndY=2.65295e-05 EndZ=0
    g2: LineSegment StartX=-4.5 StartY=2.65295e-05 StartZ=0 EndX=-2.25002 EndY=-3.8971 EndZ=0
    g3: LineSegment StartX=-2.25002 StartY=-3.8971 StartZ=0 EndX=2.24998 EndY=-3.89713 EndZ=0
    g4: LineSegment StartX=2.24998 StartY=-3.89713 StartZ=0 EndX=4.5 EndY=-2.65295e-05 EndZ=0
    g5: LineSegment StartX=4.5 StartY=-2.65295e-05 StartZ=0 EndX=2.25002 EndY=3.8971 EndZ=0
    g6: Circle [constr] CenterX=0 CenterY=0 CenterZ=0 NormalX=0 NormalY=0 NormalZ=1 AngleXU=0 Radius=4.5
  constraints (16):
    c: Coincident(g0,g1)
    c: Coincident(g1,g2)
    c: Coincident(g2,g3)
    c: Coincident(g3,g4)
    c: Coincident(g4,g5)
    c: Coincident(g5,g0)
    c: Equal(g0, g1-g5) x5
    c: PointOnObject(g0,g6)
    c: PointOnObject(g1,g6)
    c: PointOnObject(g2,g6)
    c: PointOnObject(g3,g6)
    c: PointOnObject(g4,g6)
    c: PointOnObject(g5,g6)
    c: Coincident(g6,g-1)
    c: Radius(g6) = 4.5
    c: DistanceX(g0,g0) = 4.5
FEATURE [Part::Extrusion] Extrude204  label="m4NutCut2"
  Base = -> Sketch428
  Dir = (-1,0,0)
  DirMode = 2
  FaceMakerClass = Part::FaceMakerBullseye
  FaceMakerMode = 3
  LengthFwd = 3
  LengthRev = 0
  Placement = pos=(-40,217,60.25) rot=(0,0,1;0rad)
  Solid = true
  Symmetric = false
FEATURE [Sketcher::SketchObject] Sketch429
  ArcFitTolerance = 1e-06
  FullyConstrained = true
  MakeInternals = false
  Placement = pos=(0,0,0) rot=(-0.57735,0.57735,0.57735;4.18879rad)
  sketch-geometry (7):
    g0: LineSegment StartX=2.25002 StartY=3.8971 StartZ=0 EndX=-2.24998 EndY=3.89713 EndZ=0
    g1: LineSegment StartX=-2.24998 StartY=3.89713 StartZ=0 EndX=-4.5 EndY=2.65295e-05 EndZ=0
    g2: LineSegment StartX=-4.5 StartY=2.65295e-05 StartZ=0 EndX=-2.25002 EndY=-3.8971 EndZ=0
    g3: LineSegment StartX=-2.25002 StartY=-3.8971 StartZ=0 EndX=2.24998 EndY=-3.89713 EndZ=0
    g4: LineSegment StartX=2.24998 StartY=-3.89713 StartZ=0 EndX=4.5 EndY=-2.65295e-05 EndZ=0
    g5: LineSegment StartX=4.5 StartY=-2.65295e-05 StartZ=0 EndX=2.25002 EndY=3.8971 EndZ=0
    g6: Circle [constr] CenterX=0 CenterY=0 CenterZ=0 NormalX=0 NormalY=0 NormalZ=1 AngleXU=0 Radius=4.5
  constraints (16):
    c: Coincident(g0,g1)
    c: Coincident(g1,g2)
    c: Coincident(g2,g3)
    c: Coincident(g3,g4)
    c: Coincident(g4,g5)
    c: Coincident(g5,g0)
    c: Equal(g0, g1-g5) x5
    c: PointOnObject(g0,g6)
    c: PointOnObject(g1,g6)
    c: PointOnObject(g2,g6)
    c: PointOnObject(g3,g6)
    c: PointOnObject(g4,g6)
    c: PointOnObject(g5,g6)
    c: Coincident(g6,g-1)
    c: Radius(g6) = 4.5
    c: DistanceX(g0,g0) = 4.5
FEATURE [Part::Extrusion] Extrude205  label="m4NutCut3"
  Base = -> Sketch429
  Dir = (-1,0,0)
  DirMode = 2
  FaceMakerClass = Part::FaceMakerBullseye
  FaceMakerMode = 3
  LengthFwd = 3
  LengthRev = 0
  Placement = pos=(-40,242,60.25) rot=(0,0,1;0rad)
  Solid = true
  Symmetric = false
FEATURE [Part::MultiFuse] Fusion301  label="m4nutcut"
  Refine = true
  Shapes = -> [Extrude203,Extrude204,Extrude205]
FEATURE [Part::Feature] Part__Feature238  label="m4Nut2"
  Placement = pos=(-41.25,217,60.25) rot=(0,1,0;4.71239rad)
  shape: bbox 3.764 x 8.084 x 8.084 mm, 38 faces (baked)
FEATURE [Part::Feature] Part__Feature239  label="m4Nut3"
  Placement = pos=(-41.25,242,60.25) rot=(0,1,0;4.71239rad)
  shape: bbox 3.764 x 8.084 x 8.084 mm, 38 faces (baked)
FEATURE [Part::MultiFuse] Fusion302  label="m4ScrewNuts"
  Refine = true
  Shapes = -> [Part__Feature233,Part__Feature234,Part__Feature235,Part__Feature236,Part__Feature238,Part__Feature239]
FEATURE [Part::MultiFuse] Fusion303  label="m4ScrewCut"
  Refine = true
  Shapes = -> [Cylinder068,Cylinder070,Cylinder069]
FEATURE [Part::Cut] Cut161  label="M4Screw"
  Base = -> Fusion299
  Refine = true
  Tool = -> Fusion303
FEATURE [Part::Cut] Cut162  label="M4Nut"
  Base = -> Cut161
  Refine = true
  Tool = -> Fusion301
FEATURE [Part::Feature] Part__Feature  label="m3HeatsetB"
  Placement = pos=(-102,217,90.5) rot=(0,1,0;4.71239rad)
  shape: bbox 4.684 x 5.56 x 5.56 mm, 233 faces (baked)
FEATURE [Part::Feature] Part__Feature240  label="m3HeatsetT"
  Placement = pos=(-102,217,161.5) rot=(0,1,0;4.71239rad)
  shape: bbox 4.684 x 5.56 x 5.56 mm, 233 faces (baked)
FEATURE [Part::Feature] Part__Feature241  label="m3HeatsetL"
  Placement = pos=(-102,252.5,126) rot=(0,1,0;4.71239rad)
  shape: bbox 4.684 x 5.56 x 5.56 mm, 233 faces (baked)
FEATURE [Part::Feature] Part__Feature242  label="m3HeatsetR"
  Placement = pos=(-102,181.5,126) rot=(0,1,0;4.71239rad)
  shape: bbox 4.684 x 5.56 x 5.56 mm, 233 faces (baked)
FEATURE [Part::MultiFuse] Fusion304  label="m3Heatsets"
  Refine = true
  Shapes = -> [Part__Feature,Part__Feature240,Part__Feature241,Part__Feature242]
FEATURE [Sketcher::SketchObject] Sketch430
  ArcFitTolerance = 1e-06
  FullyConstrained = true
  MakeInternals = false
  MapMode = 4
  Placement = pos=(0,0,0) rot=(0.57735,0.57735,0.57735;2.0944rad)
  sketch-geometry (4):
    g0: Circle CenterX=217 CenterY=90.5 CenterZ=0 NormalX=0 NormalY=0 NormalZ=1 AngleXU=0 Radius=1.625
    g1: Circle CenterX=252.5 CenterY=126 CenterZ=0 NormalX=0 NormalY=0 NormalZ=1 AngleXU=0 Radius=1.625
    g2: Circle CenterX=217 CenterY=161.5 CenterZ=0 NormalX=0 NormalY=0 NormalZ=1 AngleXU=0 Radius=1.625
    g3: Circle CenterX=181.5 CenterY=126 CenterZ=0 NormalX=0 NormalY=0 NormalZ=1 AngleXU=0 Radius=1.625
  constraints (12):
    c: Equal(g0,g1)
    c: Equal(g0,g2)
    c: Equal(g0,g3)
    c: Diameter(g0) = 3.25
    c: DistanceY(g-1,g0) = 90.5
    c: Distance(g0,g-2) = 217
    c: Distance(g3,g-2) = 181.5
    c: DistanceX(g-1,g1) = 252.5
    c: Vertical(g0,g2)
    c: Horizontal(g3,g1)
    c: Distance(g3,g-1) = 126
    c: Distance(g2,g-1) = 161.5
FEATURE [Part::Extrusion] Extrude206  label="m3HeatsetHoles"
  Base = -> Sketch430
  Dir = (1,0,0)
  DirMode = 2
  FaceMakerClass = Part::FaceMakerBullseye
  FaceMakerMode = 3
  LengthFwd = 20
  LengthRev = 0
  Placement = pos=(-104,0,0) rot=(0,0,1;0rad)
  Solid = true
  Symmetric = false
FEATURE [Part::Cut] Cut163  label="m3heatset"
  Base = -> Cut162
  Refine = true
  Tool = -> Extrude206
FEATURE [Part::Fillet] Fillet  label="CylFillet"
  Base = -> Cut163
  EdgeLinks = -> Cut163 [Edge1,Edge2,Edge3,Edge163,Edge164,Edge165,Edge166,Edge167,Edge168,Edge169,Edge170,Edge171,Edge172,Edge173,Edge174,Edge175,Edge176,Edge177,Edge178,Edge179]
  Edges = 20 edges: [Edge1 r=3,Edge2 r=1,Edge3 r=5,Edge163 r=5,Edge164 r=1,Edge165 r=1,Edge166 r=1,Edge167 r=1,Edge168 r=1,Edge169 r=1,Edge170 r=1,Edge171 r=1,Edge172 r=1,Edge173 r=1,Edge174 r=1,Edge175 r=1,Edge176 r=1,Edge177 r=1,Edge178 r=1,Edge179 r=1]
FEATURE [Part::Feature] Part__Feature243  label="m3_25_01"
  Placement = pos=(-99,217,161.5) rot=(0,1,0;4.71239rad)
  shape: bbox 28.29 x 5.501 x 5.501 mm, 108 faces (baked)
FEATURE [Part::Feature] Part__Feature244  label="m3_25_002"
  Placement = pos=(-99,252.5,126) rot=(0,1,0;4.71239rad)
  shape: bbox 28.29 x 5.501 x 5.501 mm, 108 faces (baked)
FEATURE [Part::Feature] Part__Feature245  label="m3_25_003"
  Placement = pos=(-99,217,90.5) rot=(0,1,0;4.71239rad)
  shape: bbox 28.29 x 5.501 x 5.501 mm, 108 faces (baked)
FEATURE [Part::Feature] Part__Feature246  label="m3_25_004"
  Placement = pos=(-99,181.5,126) rot=(0,1,0;4.71239rad)
  shape: bbox 28.29 x 5.501 x 5.501 mm, 108 faces (baked)
FEATURE [Part::MultiFuse] Fusion305  label="m3_screws"
  Refine = true
  Shapes = -> [Part__Feature243,Part__Feature244,Part__Feature245,Part__Feature246]
FEATURE [Sketcher::SketchObject] Sketch431
  ArcFitTolerance = 1e-06
  AttachmentSupport = -> [Fusion022]
  FullyConstrained = true
  MakeInternals = false
  MapMode = 2
  Placement = pos=(-107.5,217,126) rot=(0,-1,0;1.5708rad)
  sketch-geometry (16):
    g0: LineSegment StartX=-3.25 StartY=-32 StartZ=0 EndX=-3.25 EndY=-50 EndZ=0
    g1: LineSegment StartX=-3.25 StartY=-50 StartZ=0 EndX=3.25 EndY=-50 EndZ=0
    g2: LineSegment StartX=3.25 StartY=-50 StartZ=0 EndX=3.25 EndY=-32 EndZ=0
    g3: LineSegment StartX=3.25 StartY=-32 StartZ=0 EndX=-3.25 EndY=-32 EndZ=0
    g4: LineSegment StartX=-3.25 StartY=32 StartZ=0 EndX=3.25 EndY=32 EndZ=0
    g5: LineSegment StartX=3.25 StartY=32 StartZ=0 EndX=3.25 EndY=50 EndZ=0
    g6: LineSegment StartX=3.25 StartY=50 StartZ=0 EndX=-3.25 EndY=50 EndZ=0
    g7: LineSegment StartX=-3.25 StartY=50 StartZ=0 EndX=-3.25 EndY=32 EndZ=0
    g8: LineSegment StartX=32 StartY=-3.25 StartZ=0 EndX=50 EndY=-3.25 EndZ=0
    g9: LineSegment StartX=50 StartY=-3.25 StartZ=0 EndX=50 EndY=3.25 EndZ=0
    g10: LineSegment StartX=50 StartY=3.25 StartZ=0 EndX=32 EndY=3.25 EndZ=0
    g11: LineSegment StartX=32 StartY=3.25 StartZ=0 EndX=32 EndY=-3.25 EndZ=0
    g12: LineSegment StartX=-32 StartY=-3.25 StartZ=0 EndX=-32 EndY=3.25 EndZ=0
    g13: LineSegment StartX=-32 StartY=3.25 StartZ=0 EndX=-50 EndY=3.25 EndZ=0
    g14: LineSegment StartX=-50 StartY=3.25 StartZ=0 EndX=-50 EndY=-3.25 EndZ=0
    g15: LineSegment StartX=-50 StartY=-3.25 StartZ=0 EndX=-32 EndY=-3.25 EndZ=0
  constraints (44):
    c: Coincident(g0,g1)
    c: Coincident(g1,g2)
    c: Coincident(g2,g3)
    c: Coincident(g3,g0)
    c: Vertical(g0)
    c: Vertical(g2)
    c: Horizontal(g1)
    c: Symmetric(g2,g0,g-2)
    c: DistanceY(g0,g0) = 18
    c: Distance(g1,g1) = 6.5
    c: Distance(g2,g-1) = 32
    c: Coincident(g4,g5)
    c: Coincident(g5,g6)
    c: Coincident(g6,g7)
    c: Coincident(g7,g4)
    c: Horizontal(g6)
    c: Vertical(g5)
    c: Vertical(g7)
    c: Coincident(g8,g9)
    c: Coincident(g9,g10)
    c: Coincident(g10,g11)
    c: Coincident(g11,g8)
    c: Horizontal(g8)
    c: Horizontal(g10)
    c: Vertical(g9)
    c: Coincident(g12,g13)
    c: Coincident(g13,g14)
    c: Coincident(g14,g15)
    c: Coincident(g15,g12)
    c: Vertical(g14)
    c: Horizontal(g13)
    c: Horizontal(g15)
    c: Distance(g10,g10) = 18
    c: Distance(g9,g9) = 6.5
    c: Symmetric(g8,g10,g-1)
    c: DistanceX(g-1,g8) = 32
    c: DistanceY(g5,g5) = 18
    c: Distance(g6,g6) = 6.5
    c: DistanceY(g-1,g4) = 32
    c: Symmetric(g4,g4,g-2)
    c: Symmetric(g12,g12,g-1)
    c: Distance(g12,g-2) = 32
    c: Distance(g15,g15) = 18
    c: Distance(g14,g14) = 6.5
FEATURE [Part::Feature] Part__Feature247  label="m3_nut_001"
  Placement = pos=(-92,217,90.5) rot=(0,-1,0;1.5708rad)
  shape: bbox 2.772 x 6.352 x 6.352 mm, 37 faces (baked)
FEATURE [Part::Feature] Part__Feature248  label="m3_nut_002"
  Placement = pos=(-92,181.5,126) rot=(0,-1,0;1.5708rad)
  shape: bbox 2.772 x 6.352 x 6.352 mm, 37 faces (baked)
FEATURE [Part::Feature] Part__Feature249  label="m3_nut_003"
  Placement = pos=(-92,217,161.5) rot=(0,-1,0;1.5708rad)
  shape: bbox 2.772 x 6.352 x 6.352 mm, 37 faces (baked)
FEATURE [Part::Feature] Part__Feature250  label="m3_nut_004"
  Placement = pos=(-92,252.5,126) rot=(0,-1,0;1.5708rad)
  shape: bbox 2.772 x 6.352 x 6.352 mm, 37 faces (baked)
FEATURE [Part::MultiFuse] Fusion306  label="m3_nuts"
  Refine = true
  Shapes = -> [Part__Feature247,Part__Feature248,Part__Feature249,Part__Feature250]
FEATURE [Part::Extrusion] Extrude207  label="sidecut"
  Base = -> Sketch431
  Dir = (-1,0,2e-16)
  DirMode = 2
  FaceMakerClass = Part::FaceMakerBullseye
  FaceMakerMode = 3
  LengthFwd = 4
  LengthRev = 0
  Placement = pos=(17.5,0,0) rot=(0,0,1;0rad)
  Solid = true
  Symmetric = false
FEATURE [Part::Cut] Cut164  label="OuterHolder"
  Base = -> Fillet
  Refine = true
  Tool = -> Extrude207
FEATURE [Part::Fillet] Fillet001  label="CameraHolder"
  Base = -> Cut164
  EdgeLinks = -> Cut164 [Edge28,Edge30,Edge31,Edge32,Edge33,Edge34,Edge35,Edge36,Edge39,Edge40,Edge41,Edge42,Edge43,Edge44,Edge45,Edge47,Edge113,Edge130,Edge132,Edge152,Edge154,Edge169]
  Edges = 22 edges: [Edge28 r=1,Edge30 r=3,Edge31 r=1,Edge32 r=3,Edge33 r=3,Edge34 r=3,Edge35 r=1,Edge36 r=1,Edge39 r=1,Edge40 r=1,Edge41 r=3,Edge42 r=3,Edge43 r=3,Edge44 r=1,Edge45 r=3,Edge47 r=1,Edge113 r=1,Edge130 r=1,Edge132 r=1,Edge152 r=1,Edge154 r=1,Edge169 r=1]
FEATURE [App::Part] Part  label="CamHolder001"
  Group = -> [Fusion001,Fusion,Fusion003,Fusion002,Fusion005,Fusion006,Fusion007,Fusion004,Cylinder,Cylinder008,Cylinder009,Cylinder010,Cylinder003,Cylinder028,Cylinder025,Cylinder026,Cylinder027,Cylinder029,Cylinder033,Cylinder032,Cylinder031,Cylinder030,Cylinder035,Cylinder034,Cylinder038,Cylinder040,Cylinder036,Cylinder037,Cylinder039,Cylinder042,Cylinder041,Cylinder016,Cylinder020,Cylinder017,Cylinder018,+114 more]
  Origin = -> Origin
